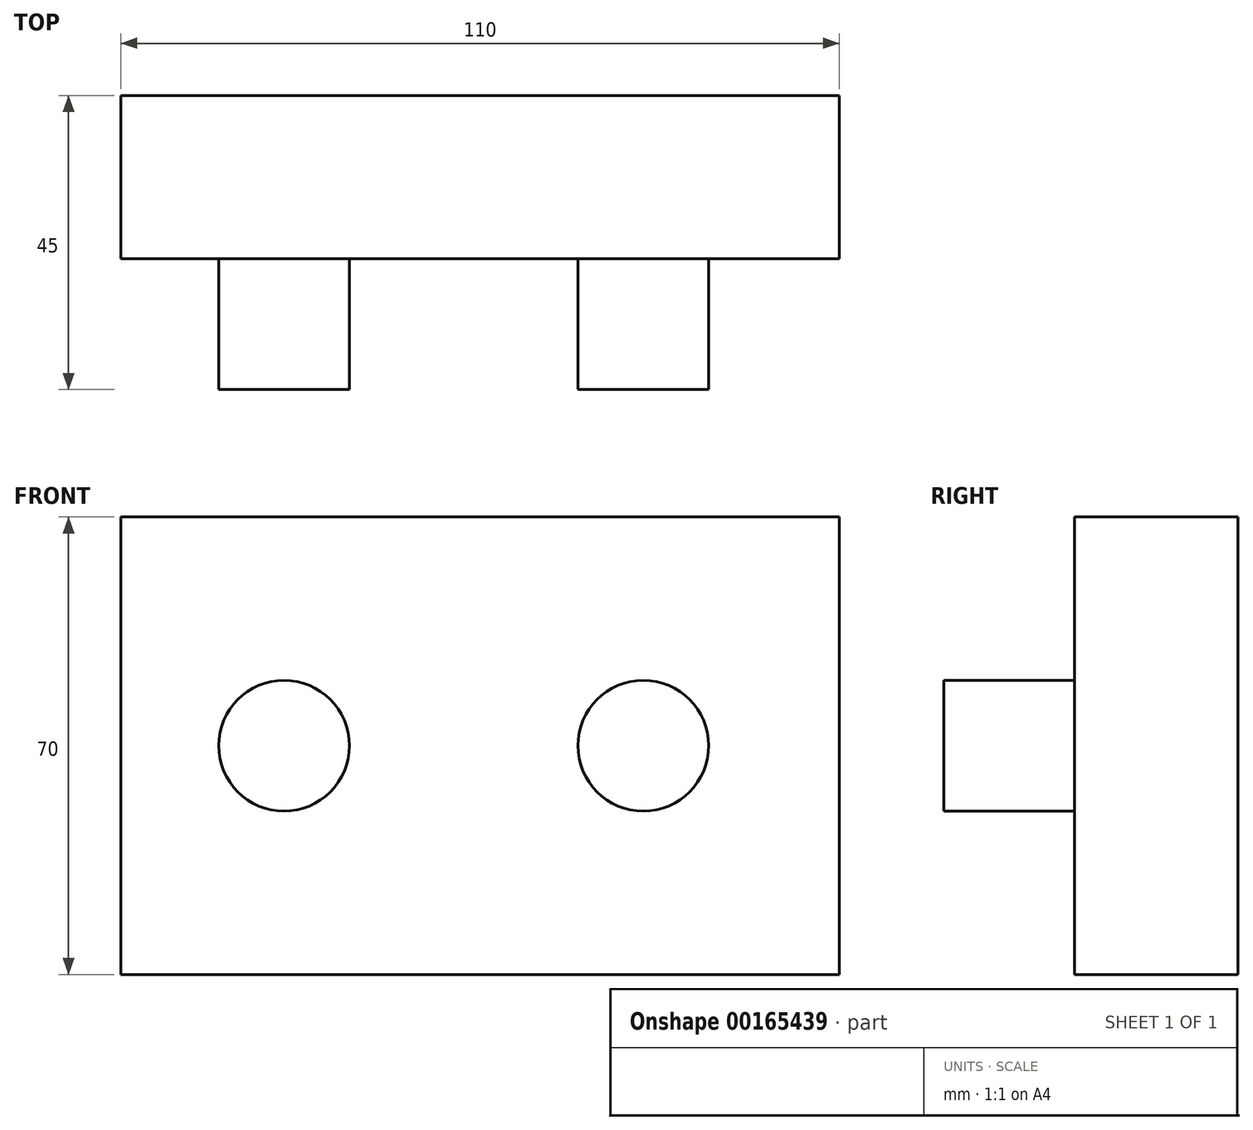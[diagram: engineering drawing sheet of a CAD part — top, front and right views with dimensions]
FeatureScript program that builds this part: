
annotation { "Feature Type Name" : "Feature", "Feature Type Description" : "" }
export const myFeature = defineFeature(function(context is Context, id is Id, definition is map)
    precondition{}
    {
        {
            var Q0;
            Q0=qCreatedBy(makeId("Front.planeOp"),FACE);
            var sketch = newSketch(context, id + "F0", { "sketchPlane" : qUnion([Q0])});
            skLineSegment(sketch, "E0.bottom", {"start": v(0, 0) * mm, "end": v(110, 0) * mm});
            skLineSegment(sketch, "E0.top", {"start": v(0, 70) * mm, "end": v(110, 70) * mm});
            skLineSegment(sketch, "E0.left", {"start": v(0, 0) * mm, "end": v(0, 70) * mm});
            skLineSegment(sketch, "E0.right", {"start": v(110, 0) * mm, "end": v(110, 70) * mm});
            skSolve(sketch);
        }
        {
            var Q0;
            Q0=makeQuery(id+"F0.imprint","IMPRINT",FACE,{"disambiguationData":[TD([[makeQuery(id+"F0.imprint","IMPRINT",EDGE,{"derivedFrom":sQuery(id+"F0.wireOp",EDGE,"E0.bottom")}),1.0]])]});
            extrude(context, id + "F1", {"entities" : qUnion([Q0]), "depth" : 25 * mm});
        }
        {
            var Q0;
            Q0=makeQuery(id+"F1.opExtrude","CAP_FACE",FACE,{"disambiguationData":[OSD([sQuery(id+"F0.wireOp",EDGE,"E0.bottom"),sQuery(id+"F0.wireOp",EDGE,"E0.top"),sQuery(id+"F0.wireOp",EDGE,"E0.left"),sQuery(id+"F0.wireOp",EDGE,"E0.right")])],"isStart":false});
            var sketch = newSketch(context, id + "F2", { "sketchPlane" : qUnion([Q0])});
            skCircle(sketch, "E1", {"center": v(25, 35) * mm, "radius": 10 * mm});
            skPoint(sketch, "E1.centerSnap0", {"position": v(0, 35) * mm});
            skCircle(sketch, "E2", {"center": v(80, 35) * mm, "radius": 10 * mm});
            skPoint(sketch, "E2.centerSnap0", {"position": v(110, 35) * mm});
            skLineSegment(sketch, "E3", {"start": v(25, 35) * mm, "end": v(80, 35) * mm});
            skSolve(sketch);
        }
        {
            var Q0;
            Q0=makeQuery(id+"F2.imprint","IMPRINT",FACE,{"disambiguationData":[TD([[makeQuery(id+"F2.imprint","IMPRINT",EDGE,{"derivedFrom":sQuery(id+"F2.wireOp",EDGE,"E1")}),1.0]])]});
            var Q1;
            Q1=makeQuery(id+"F2.imprint","IMPRINT",FACE,{"disambiguationData":[TD([[makeQuery(id+"F2.imprint","IMPRINT",EDGE,{"derivedFrom":sQuery(id+"F2.wireOp",EDGE,"E2")}),1.0]])]});
            extrude(context, id + "F3", {"entities" : qUnion([Q0, Q1]), "operationType" : NewBodyOperationType.ADD, "depth" : 20 * mm});
        }
    });
